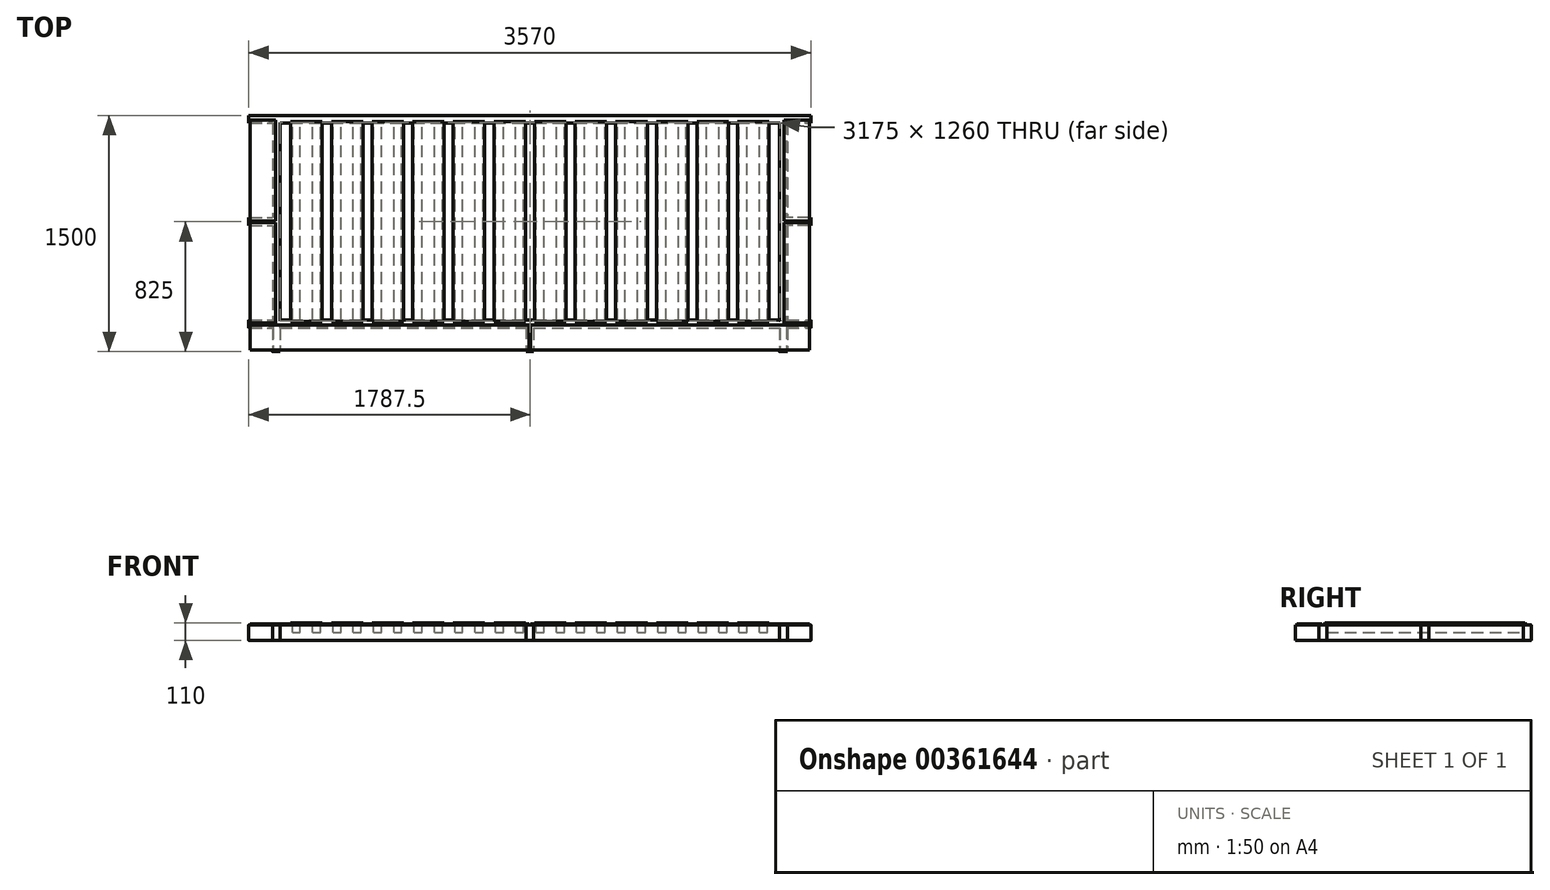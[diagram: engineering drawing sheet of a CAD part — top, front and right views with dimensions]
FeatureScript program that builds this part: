
annotation { "Feature Type Name" : "Feature", "Feature Type Description" : "" }
export const myFeature = defineFeature(function(context is Context, id is Id, definition is map)
    precondition{}
    {
        {
            var Q0;
            Q0=qCreatedBy(makeId("Top.planeOp"),FACE);
            var sketch = newSketch(context, id + "F0", { "sketchPlane" : qUnion([Q0])});
            skLineSegment(sketch, "E0.bottom", {"start": v(0, 0) * mm, "end": v(150, 0) * mm});
            skLineSegment(sketch, "E0.top", {"start": v(0, 50) * mm, "end": v(150, 50) * mm});
            skLineSegment(sketch, "E0.left", {"start": v(0, 0) * mm, "end": v(0, 50) * mm});
            skLineSegment(sketch, "E0.right", {"start": v(3570, 0) * mm, "end": v(3570, 50) * mm});
            skLineSegment(sketch, "E1.bottom", {"start": v(0, 1350) * mm, "end": v(3570, 1350) * mm});
            skLineSegment(sketch, "E1.left", {"start": v(0, 1350) * mm, "end": v(0, 1300) * mm});
            skLineSegment(sketch, "E1.right", {"start": v(3570, 1350) * mm, "end": v(3570, 1300) * mm});
            skLineSegment(sketch, "E2.trimOffspring", {"start": v(0, 1300) * mm, "end": v(150, 1300) * mm});
            skLineSegment(sketch, "E3.top", {"start": v(150, -150) * mm, "end": v(200, -150) * mm});
            skLineSegment(sketch, "E4.top", {"start": v(3370, -150) * mm, "end": v(3420, -150) * mm});
            skLineSegment(sketch, "E4.left", {"start": v(3370, 1300) * mm, "end": v(3370, 50) * mm});
            skLineSegment(sketch, "E4.right", {"start": v(3420, 1300) * mm, "end": v(3420, 50) * mm});
            skLineSegment(sketch, "E5.trimOffspring", {"start": v(3420, 0) * mm, "end": v(3570, 0) * mm});
            skLineSegment(sketch, "E6.trimOffspring", {"start": v(3420, 50) * mm, "end": v(3570, 50) * mm});
            skLineSegment(sketch, "E7.trimOffspring", {"start": v(3370, 0) * mm, "end": v(3370, -150) * mm});
            skLineSegment(sketch, "E8.trimOffspring", {"start": v(3420, 0) * mm, "end": v(3420, -150) * mm});
            skLineSegment(sketch, "E9.trimOffspring", {"start": v(3420, 1300) * mm, "end": v(3570, 1300) * mm});
            skLineSegment(sketch, "E10.trimOffspring", {"start": v(200, 1300) * mm, "end": v(3370, 1300) * mm});
            skLineSegment(sketch, "E11.trimOffspring", {"start": v(200, 50) * mm, "end": v(3370, 50) * mm});
            skLineSegment(sketch, "E12.trimOffspring", {"start": v(200, 0) * mm, "end": v(200, -150) * mm});
            skLineSegment(sketch, "E13.trimOffspring", {"start": v(150, 0) * mm, "end": v(150, -150) * mm});
            skLineSegment(sketch, "E14.trimOffspring", {"start": v(200, 0) * mm, "end": v(1760, 0) * mm});
            skLineSegment(sketch, "E15.bottom", {"start": v(0, 700) * mm, "end": v(150, 700) * mm});
            skLineSegment(sketch, "E15.left", {"start": v(0, 700) * mm, "end": v(0, 675) * mm});
            skPoint(sketch, "E16.startSnap0", {"position": v(1785, 1350) * mm});
            skLineSegment(sketch, "E17.trimOffspring", {"start": v(150, 675) * mm, "end": v(2226.14, 675) * mm, "construction": true});
            skLineSegment(sketch, "E18.MirrorCS", {"start": v(0, 650) * mm, "end": v(0, 675) * mm});
            skLineSegment(sketch, "E19.MirrorCS", {"start": v(0, 650) * mm, "end": v(150, 650) * mm});
            skLineSegment(sketch, "E20.MirrorCS", {"start": v(3570, 650) * mm, "end": v(3420, 650) * mm});
            skLineSegment(sketch, "E21.MirrorCS", {"start": v(3570, 700) * mm, "end": v(3570, 675) * mm});
            skLineSegment(sketch, "E22.MirrorCS", {"start": v(3570, 650) * mm, "end": v(3570, 675) * mm});
            skLineSegment(sketch, "E23.MirrorCS", {"start": v(3570, 700) * mm, "end": v(3420, 700) * mm});
            skLineSegment(sketch, "E24.top", {"start": v(1760, -150) * mm, "end": v(1810, -150) * mm});
            skLineSegment(sketch, "E24.left", {"start": v(1760, 0) * mm, "end": v(1760, -150) * mm});
            skLineSegment(sketch, "E24.right", {"start": v(1810, 0) * mm, "end": v(1810, -150) * mm});
            skLineSegment(sketch, "E25.trimOffspring", {"start": v(1810, 0) * mm, "end": v(3370, 0) * mm});
            skLineSegment(sketch, "E26", {"start": v(150, 1300) * mm, "end": v(150, 50) * mm});
            skLineSegment(sketch, "E27", {"start": v(200, 50) * mm, "end": v(200, 1300) * mm});
            skSolve(sketch);
        }
        {
            var Q0;
            Q0=qSketchRegion(id+"F0",true);
            var Q1;
            {var subQ0=sQuery(id+"F0.wireOp",EDGE,"04053e72-1d3c-4b0a-b337-873e80f4f36b.1.0.0");Q1=makeQuery(id+"F0.imprint","IMPRINT",FACE,{"disambiguationData":[TD([[makeQuery(id+"F0.imprint","IMPRINT",EDGE,{"derivedFrom":subQ0}),1.0]])]});}
            var Q2;
            {var subQ0=sQuery(id+"F0.wireOp",EDGE,"04053e72-1d3c-4b0a-b337-873e80f4f36b.2.0.0");Q2=makeQuery(id+"F0.imprint","IMPRINT",FACE,{"disambiguationData":[TD([[makeQuery(id+"F0.imprint","IMPRINT",EDGE,{"derivedFrom":subQ0}),1.0]])]});}
            var Q3;
            {var subQ0=sQuery(id+"F0.wireOp",EDGE,"04053e72-1d3c-4b0a-b337-873e80f4f36b.3.0.0");Q3=makeQuery(id+"F0.imprint","IMPRINT",FACE,{"disambiguationData":[TD([[makeQuery(id+"F0.imprint","IMPRINT",EDGE,{"derivedFrom":subQ0}),1.0]])]});}
            var Q4;
            {var subQ0=sQuery(id+"F0.wireOp",EDGE,"04053e72-1d3c-4b0a-b337-873e80f4f36b.4.0.0");Q4=makeQuery(id+"F0.imprint","IMPRINT",FACE,{"disambiguationData":[TD([[makeQuery(id+"F0.imprint","IMPRINT",EDGE,{"derivedFrom":subQ0}),1.0]])]});}
            var Q5;
            {var subQ0=sQuery(id+"F0.wireOp",EDGE,"04053e72-1d3c-4b0a-b337-873e80f4f36b.5.0.0");Q5=makeQuery(id+"F0.imprint","IMPRINT",FACE,{"disambiguationData":[TD([[makeQuery(id+"F0.imprint","IMPRINT",EDGE,{"derivedFrom":subQ0}),1.0]])]});}
            var Q6;
            {var subQ0=sQuery(id+"F0.wireOp",EDGE,"04053e72-1d3c-4b0a-b337-873e80f4f36b.6.0.0");Q6=makeQuery(id+"F0.imprint","IMPRINT",FACE,{"disambiguationData":[TD([[makeQuery(id+"F0.imprint","IMPRINT",EDGE,{"derivedFrom":subQ0}),1.0]])]});}
            var Q7;
            {var subQ0=sQuery(id+"F0.wireOp",EDGE,"04053e72-1d3c-4b0a-b337-873e80f4f36b.7.0.0");Q7=makeQuery(id+"F0.imprint","IMPRINT",FACE,{"disambiguationData":[TD([[makeQuery(id+"F0.imprint","IMPRINT",EDGE,{"derivedFrom":subQ0}),1.0]])]});}
            var Q8;
            {var subQ0=sQuery(id+"F0.wireOp",EDGE,"04053e72-1d3c-4b0a-b337-873e80f4f36b.8.0.0");Q8=makeQuery(id+"F0.imprint","IMPRINT",FACE,{"disambiguationData":[TD([[makeQuery(id+"F0.imprint","IMPRINT",EDGE,{"derivedFrom":subQ0}),1.0]])]});}
            var Q9;
            {var subQ0=sQuery(id+"F0.wireOp",EDGE,"04053e72-1d3c-4b0a-b337-873e80f4f36b.9.0.0");Q9=makeQuery(id+"F0.imprint","IMPRINT",FACE,{"disambiguationData":[TD([[makeQuery(id+"F0.imprint","IMPRINT",EDGE,{"derivedFrom":subQ0}),1.0]])]});}
            var Q10;
            {var subQ0=sQuery(id+"F0.wireOp",EDGE,"04053e72-1d3c-4b0a-b337-873e80f4f36b.10.0.0");Q10=makeQuery(id+"F0.imprint","IMPRINT",FACE,{"disambiguationData":[TD([[makeQuery(id+"F0.imprint","IMPRINT",EDGE,{"derivedFrom":subQ0}),1.0]])]});}
            var Q11;
            {var subQ0=sQuery(id+"F0.wireOp",EDGE,"04053e72-1d3c-4b0a-b337-873e80f4f36b.11.0.0");Q11=makeQuery(id+"F0.imprint","IMPRINT",FACE,{"disambiguationData":[TD([[makeQuery(id+"F0.imprint","IMPRINT",EDGE,{"derivedFrom":subQ0}),1.0]])]});}
            var Q12;
            {var subQ0=sQuery(id+"F0.wireOp",EDGE,"04053e72-1d3c-4b0a-b337-873e80f4f36b.12.0.0");Q12=makeQuery(id+"F0.imprint","IMPRINT",FACE,{"disambiguationData":[TD([[makeQuery(id+"F0.imprint","IMPRINT",EDGE,{"derivedFrom":subQ0}),1.0]])]});}
            var Q13;
            {var subQ0=sQuery(id+"F0.wireOp",EDGE,"04053e72-1d3c-4b0a-b337-873e80f4f36b.13.0.0");Q13=makeQuery(id+"F0.imprint","IMPRINT",FACE,{"disambiguationData":[TD([[makeQuery(id+"F0.imprint","IMPRINT",EDGE,{"derivedFrom":subQ0}),1.0]])]});}
            var Q14;
            {var subQ0=sQuery(id+"F0.wireOp",EDGE,"04053e72-1d3c-4b0a-b337-873e80f4f36b.14.0.0");Q14=makeQuery(id+"F0.imprint","IMPRINT",FACE,{"disambiguationData":[TD([[makeQuery(id+"F0.imprint","IMPRINT",EDGE,{"derivedFrom":subQ0}),1.0]])]});}
            var Q15;
            {var subQ0=sQuery(id+"F0.wireOp",EDGE,"04053e72-1d3c-4b0a-b337-873e80f4f36b.15.0.0");Q15=makeQuery(id+"F0.imprint","IMPRINT",FACE,{"disambiguationData":[TD([[makeQuery(id+"F0.imprint","IMPRINT",EDGE,{"derivedFrom":subQ0}),1.0]])]});}
            var Q16;
            {var subQ0=sQuery(id+"F0.wireOp",EDGE,"04053e72-1d3c-4b0a-b337-873e80f4f36b.16.0.0");Q16=makeQuery(id+"F0.imprint","IMPRINT",FACE,{"disambiguationData":[TD([[makeQuery(id+"F0.imprint","IMPRINT",EDGE,{"derivedFrom":subQ0}),1.0]])]});}
            var Q17;
            {var subQ0=sQuery(id+"F0.wireOp",EDGE,"04053e72-1d3c-4b0a-b337-873e80f4f36b.17.0.0");Q17=makeQuery(id+"F0.imprint","IMPRINT",FACE,{"disambiguationData":[TD([[makeQuery(id+"F0.imprint","IMPRINT",EDGE,{"derivedFrom":subQ0}),1.0]])]});}
            var Q18;
            {var subQ0=sQuery(id+"F0.wireOp",EDGE,"04053e72-1d3c-4b0a-b337-873e80f4f36b.18.0.0");Q18=makeQuery(id+"F0.imprint","IMPRINT",FACE,{"disambiguationData":[TD([[makeQuery(id+"F0.imprint","IMPRINT",EDGE,{"derivedFrom":subQ0}),1.0]])]});}
            var Q19;
            {var subQ0=sQuery(id+"F0.wireOp",EDGE,"04053e72-1d3c-4b0a-b337-873e80f4f36b.19.0.0");Q19=makeQuery(id+"F0.imprint","IMPRINT",FACE,{"disambiguationData":[TD([[makeQuery(id+"F0.imprint","IMPRINT",EDGE,{"derivedFrom":subQ0}),1.0]])]});}
            var Q20;
            {var subQ0=sQuery(id+"F0.wireOp",EDGE,"83652a9d-b2ed-44b6-aa75-f454ae2646cd.0.20.0");Q20=makeQuery(id+"F0.imprint","IMPRINT",FACE,{"disambiguationData":[TD([[makeQuery(id+"F0.imprint","IMPRINT",EDGE,{"derivedFrom":subQ0}),1.0]])]});}
            var Q21;
            {var subQ0=sQuery(id+"F0.wireOp",EDGE,"83652a9d-b2ed-44b6-aa75-f454ae2646cd.0.21.0");Q21=makeQuery(id+"F0.imprint","IMPRINT",FACE,{"disambiguationData":[TD([[makeQuery(id+"F0.imprint","IMPRINT",EDGE,{"derivedFrom":subQ0}),1.0]])]});}
            var Q22;
            {var subQ0=sQuery(id+"F0.wireOp",EDGE,"83652a9d-b2ed-44b6-aa75-f454ae2646cd.0.22.0");Q22=makeQuery(id+"F0.imprint","IMPRINT",FACE,{"disambiguationData":[TD([[makeQuery(id+"F0.imprint","IMPRINT",EDGE,{"derivedFrom":subQ0}),1.0]])]});}
            var Q23;
            {var subQ0=sQuery(id+"F0.wireOp",EDGE,"83652a9d-b2ed-44b6-aa75-f454ae2646cd.0.23.0");Q23=makeQuery(id+"F0.imprint","IMPRINT",FACE,{"disambiguationData":[TD([[makeQuery(id+"F0.imprint","IMPRINT",EDGE,{"derivedFrom":subQ0}),1.0]])]});}
            var Q24;
            {var subQ0=sQuery(id+"F0.wireOp",EDGE,"83652a9d-b2ed-44b6-aa75-f454ae2646cd.0.24.0");Q24=makeQuery(id+"F0.imprint","IMPRINT",FACE,{"disambiguationData":[TD([[makeQuery(id+"F0.imprint","IMPRINT",EDGE,{"derivedFrom":subQ0}),1.0]])]});}
            var Q25;
            {var subQ0=sQuery(id+"F0.wireOp",EDGE,"83652a9d-b2ed-44b6-aa75-f454ae2646cd.0.25.0");Q25=makeQuery(id+"F0.imprint","IMPRINT",FACE,{"disambiguationData":[TD([[makeQuery(id+"F0.imprint","IMPRINT",EDGE,{"derivedFrom":subQ0}),1.0]])]});}
            extrude(context, id + "F1", {"entities" : qUnion([Q0, Q1, Q2, Q3, Q4, Q5, Q6, Q7, Q8, Q9, Q10, Q11, Q12, Q13, Q14, Q15, Q16, Q17, Q18, Q19, Q20, Q21, Q22, Q23, Q24, Q25]), "oppositeDirection" : true, "depth" : 100 * mm});
        }
        {
            var Q0;
            Q0=makeQuery(id+"FPwb0Jo6nws5QIE_0.opExtrude","CAP_EDGE",EDGE,{"disambiguationData":[OSD([sQuery(id+"F0.wireOp",EDGE,"E14.trimOffspring")])],"isStart":false});
            var Q1;
            Q1=makeQuery(id+"FPwb0Jo6nws5QIE_0.opExtrude","CAP_EDGE",EDGE,{"disambiguationData":[OSD([sQuery(id+"F0.wireOp",EDGE,"E7.trimOffspring")])],"isStart":false});
            var Q2;
            Q2=makeQuery(id+"FPwb0Jo6nws5QIE_0.opExtrude","CAP_EDGE",EDGE,{"disambiguationData":[OSD([sQuery(id+"F0.wireOp",EDGE,"E5.trimOffspring")])],"isStart":false});
            var Q3;
            Q3=makeQuery(id+"FPwb0Jo6nws5QIE_0.opExtrude","CAP_EDGE",EDGE,{"disambiguationData":[OSD([sQuery(id+"F0.wireOp",EDGE,"E8.trimOffspring")])],"isStart":false});
            var Q4;
            Q4=makeQuery(id+"FPwb0Jo6nws5QIE_0.opExtrude","CAP_EDGE",EDGE,{"disambiguationData":[OSD([sQuery(id+"F0.wireOp",EDGE,"E6.trimOffspring")])],"isStart":false});
            var Q5;
            Q5=makeQuery(id+"FPwb0Jo6nws5QIE_0.opExtrude","CAP_EDGE",EDGE,{"disambiguationData":[OSD([sQuery(id+"F0.wireOp",EDGE,"E4.right")])],"isStart":false});
            var Q6;
            Q6=makeQuery(id+"FPwb0Jo6nws5QIE_0.opExtrude","CAP_EDGE",EDGE,{"disambiguationData":[OSD([sQuery(id+"F0.wireOp",EDGE,"E4.left")])],"isStart":false});
            var Q7;
            Q7=makeQuery(id+"FPwb0Jo6nws5QIE_0.opExtrude","CAP_EDGE",EDGE,{"disambiguationData":[OSD([sQuery(id+"F0.wireOp",EDGE,"E11.trimOffspring")])],"isStart":false});
            var Q8;
            Q8=makeQuery(id+"FPwb0Jo6nws5QIE_0.opExtrude","CAP_EDGE",EDGE,{"disambiguationData":[OSD([sQuery(id+"F0.wireOp",EDGE,"E10.trimOffspring")])],"isStart":false});
            var Q9;
            Q9=makeQuery(id+"FPwb0Jo6nws5QIE_0.opExtrude","CAP_EDGE",EDGE,{"disambiguationData":[OSD([sQuery(id+"F0.wireOp",EDGE,"E1.bottom")])],"isStart":false});
            var Q10;
            Q10=makeQuery(id+"FPwb0Jo6nws5QIE_0.opExtrude","CAP_EDGE",EDGE,{"disambiguationData":[OSD([sQuery(id+"F0.wireOp",EDGE,"E9.trimOffspring")])],"isStart":false});
            var Q11;
            Q11=makeQuery(id+"FPwb0Jo6nws5QIE_0.opExtrude","CAP_EDGE",EDGE,{"disambiguationData":[OSD([sQuery(id+"F0.wireOp",EDGE,"E3.right")])],"isStart":false});
            var Q12;
            Q12=makeQuery(id+"FPwb0Jo6nws5QIE_0.opExtrude","CAP_EDGE",EDGE,{"disambiguationData":[OSD([sQuery(id+"F0.wireOp",EDGE,"E2.trimOffspring")])],"isStart":false});
            var Q13;
            Q13=makeQuery(id+"FPwb0Jo6nws5QIE_0.opExtrude","CAP_EDGE",EDGE,{"disambiguationData":[OSD([sQuery(id+"F0.wireOp",EDGE,"E3.left")])],"isStart":false});
            var Q14;
            Q14=makeQuery(id+"FPwb0Jo6nws5QIE_0.opExtrude","CAP_EDGE",EDGE,{"disambiguationData":[OSD([sQuery(id+"F0.wireOp",EDGE,"E0.top")])],"isStart":false});
            var Q15;
            Q15=makeQuery(id+"FPwb0Jo6nws5QIE_0.opExtrude","CAP_EDGE",EDGE,{"disambiguationData":[OSD([sQuery(id+"F0.wireOp",EDGE,"E0.bottom")])],"isStart":false});
            var Q16;
            Q16=makeQuery(id+"FPwb0Jo6nws5QIE_0.opExtrude","CAP_EDGE",EDGE,{"disambiguationData":[OSD([sQuery(id+"F0.wireOp",EDGE,"E13.trimOffspring")])],"isStart":false});
            var Q17;
            Q17=makeQuery(id+"FPwb0Jo6nws5QIE_0.opExtrude","CAP_EDGE",EDGE,{"disambiguationData":[OSD([sQuery(id+"F0.wireOp",EDGE,"E12.trimOffspring")])],"isStart":false});
            var Q18;
            Q18=makeQuery(id+"F1.opExtrude","CAP_EDGE",EDGE,{"disambiguationData":[OSD([sQuery(id+"F0.wireOp",EDGE,"E2.trimOffspring")])],"isStart":true});
            var Q19;
            Q19=makeQuery(id+"F1.opExtrude","CAP_EDGE",EDGE,{"disambiguationData":[OSD([sQuery(id+"F0.wireOp",EDGE,"E1.bottom")])],"isStart":true});
            var Q20;
            Q20=makeQuery(id+"F1.opExtrude","CAP_EDGE",EDGE,{"disambiguationData":[OSD([sQuery(id+"F0.wireOp",EDGE,"E10.trimOffspring")])],"isStart":true});
            var Q21;
            Q21=makeQuery(id+"F1.opExtrude","CAP_EDGE",EDGE,{"disambiguationData":[OSD([sQuery(id+"F0.wireOp",EDGE,"E3.right")])],"isStart":true});
            var Q22;
            Q22=makeQuery(id+"F1.opExtrude","CAP_EDGE",EDGE,{"disambiguationData":[OSD([sQuery(id+"F0.wireOp",EDGE,"E3.left")])],"isStart":true});
            var Q23;
            Q23=makeQuery(id+"F1.opExtrude","CAP_EDGE",EDGE,{"disambiguationData":[OSD([sQuery(id+"F0.wireOp",EDGE,"E14.trimOffspring")])],"isStart":true});
            var Q24;
            Q24=makeQuery(id+"F1.opExtrude","CAP_EDGE",EDGE,{"disambiguationData":[OSD([sQuery(id+"F0.wireOp",EDGE,"E11.trimOffspring")])],"isStart":true});
            var Q25;
            Q25=makeQuery(id+"F1.opExtrude","CAP_EDGE",EDGE,{"disambiguationData":[OSD([sQuery(id+"F0.wireOp",EDGE,"E0.top")])],"isStart":true});
            var Q26;
            Q26=makeQuery(id+"F1.opExtrude","CAP_EDGE",EDGE,{"disambiguationData":[OSD([sQuery(id+"F0.wireOp",EDGE,"E0.bottom")])],"isStart":true});
            var Q27;
            Q27=makeQuery(id+"F1.opExtrude","CAP_EDGE",EDGE,{"disambiguationData":[OSD([sQuery(id+"F0.wireOp",EDGE,"E13.trimOffspring")])],"isStart":true});
            var Q28;
            Q28=makeQuery(id+"F1.opExtrude","CAP_EDGE",EDGE,{"disambiguationData":[OSD([sQuery(id+"F0.wireOp",EDGE,"E4.left")])],"isStart":true});
            var Q29;
            Q29=makeQuery(id+"F1.opExtrude","CAP_EDGE",EDGE,{"disambiguationData":[OSD([sQuery(id+"F0.wireOp",EDGE,"E4.right")])],"isStart":true});
            var Q30;
            Q30=makeQuery(id+"F1.opExtrude","CAP_EDGE",EDGE,{"disambiguationData":[OSD([sQuery(id+"F0.wireOp",EDGE,"E6.trimOffspring")])],"isStart":true});
            var Q31;
            Q31=makeQuery(id+"F1.opExtrude","CAP_EDGE",EDGE,{"disambiguationData":[OSD([sQuery(id+"F0.wireOp",EDGE,"E5.trimOffspring")])],"isStart":true});
            var Q32;
            Q32=makeQuery(id+"F1.opExtrude","CAP_EDGE",EDGE,{"disambiguationData":[OSD([sQuery(id+"F0.wireOp",EDGE,"E8.trimOffspring")])],"isStart":true});
            var Q33;
            Q33=makeQuery(id+"F1.opExtrude","CAP_EDGE",EDGE,{"disambiguationData":[OSD([sQuery(id+"F0.wireOp",EDGE,"E7.trimOffspring")])],"isStart":true});
            var Q34;
            Q34=makeQuery(id+"F1.opExtrude","CAP_EDGE",EDGE,{"disambiguationData":[OSD([sQuery(id+"F0.wireOp",EDGE,"E9.trimOffspring")])],"isStart":true});
            fillet(context, id + "F2", {"entities" : qUnion([Q0, Q1, Q2, Q3, Q4, Q5, Q6, Q7, Q8, Q9, Q10, Q11, Q12, Q13, Q14, Q15, Q16, Q17, Q18, Q19, Q20, Q21, Q22, Q23, Q24, Q25, Q26, Q27, Q28, Q29, Q30, Q31, Q32, Q33, Q34]), "radius" : 5 * mm, "tangentPropagation" : true, "allowEdgeOverflow" : false});
        }
        {
            var Q0;
            Q0=makeQuery(id+"F1.opExtrude","CAP_EDGE",EDGE,{"disambiguationData":[OSD([sQuery(id+"F0.wireOp",EDGE,"E6.trimOffspring")])],"isStart":false});
            var Q1;
            Q1=makeQuery(id+"F1.opExtrude","CAP_EDGE",EDGE,{"disambiguationData":[OSD([sQuery(id+"F0.wireOp",EDGE,"E11.trimOffspring")])],"isStart":false});
            var Q2;
            Q2=makeQuery(id+"F1.opExtrude","CAP_EDGE",EDGE,{"disambiguationData":[OSD([sQuery(id+"F0.wireOp",EDGE,"E4.left")])],"isStart":false});
            var Q3;
            Q3=makeQuery(id+"F1.opExtrude","CAP_EDGE",EDGE,{"disambiguationData":[OSD([sQuery(id+"F0.wireOp",EDGE,"E4.right")])],"isStart":false});
            var Q4;
            Q4=makeQuery(id+"F1.opExtrude","CAP_EDGE",EDGE,{"disambiguationData":[OSD([sQuery(id+"F0.wireOp",EDGE,"E8.trimOffspring")])],"isStart":false});
            var Q5;
            Q5=makeQuery(id+"F1.opExtrude","CAP_EDGE",EDGE,{"disambiguationData":[OSD([sQuery(id+"F0.wireOp",EDGE,"E7.trimOffspring")])],"isStart":false});
            var Q6;
            Q6=makeQuery(id+"F1.opExtrude","CAP_EDGE",EDGE,{"disambiguationData":[OSD([sQuery(id+"F0.wireOp",EDGE,"E5.trimOffspring")])],"isStart":false});
            var Q7;
            Q7=makeQuery(id+"F1.opExtrude","CAP_EDGE",EDGE,{"disambiguationData":[OSD([sQuery(id+"F0.wireOp",EDGE,"E14.trimOffspring")])],"isStart":false});
            var Q8;
            Q8=makeQuery(id+"F1.opExtrude","CAP_EDGE",EDGE,{"disambiguationData":[OSD([sQuery(id+"F0.wireOp",EDGE,"E12.trimOffspring")])],"isStart":false});
            var Q9;
            Q9=makeQuery(id+"F1.opExtrude","CAP_EDGE",EDGE,{"disambiguationData":[OSD([sQuery(id+"F0.wireOp",EDGE,"E3.left")])],"isStart":false});
            var Q10;
            Q10=makeQuery(id+"F1.opExtrude","CAP_EDGE",EDGE,{"disambiguationData":[OSD([sQuery(id+"F0.wireOp",EDGE,"E3.right")])],"isStart":false});
            var Q11;
            Q11=makeQuery(id+"F1.opExtrude","CAP_EDGE",EDGE,{"disambiguationData":[OSD([sQuery(id+"F0.wireOp",EDGE,"E0.top")])],"isStart":false});
            var Q12;
            Q12=makeQuery(id+"F1.opExtrude","CAP_EDGE",EDGE,{"disambiguationData":[OSD([sQuery(id+"F0.wireOp",EDGE,"E0.bottom")])],"isStart":false});
            var Q13;
            Q13=makeQuery(id+"F1.opExtrude","CAP_EDGE",EDGE,{"disambiguationData":[OSD([sQuery(id+"F0.wireOp",EDGE,"E13.trimOffspring")])],"isStart":false});
            var Q14;
            Q14=makeQuery(id+"F1.opExtrude","CAP_EDGE",EDGE,{"disambiguationData":[OSD([sQuery(id+"F0.wireOp",EDGE,"E2.trimOffspring")])],"isStart":false});
            var Q15;
            Q15=makeQuery(id+"F1.opExtrude","CAP_EDGE",EDGE,{"disambiguationData":[OSD([sQuery(id+"F0.wireOp",EDGE,"E1.bottom")])],"isStart":false});
            var Q16;
            Q16=makeQuery(id+"F1.opExtrude","CAP_EDGE",EDGE,{"disambiguationData":[OSD([sQuery(id+"F0.wireOp",EDGE,"E10.trimOffspring")])],"isStart":false});
            var Q17;
            Q17=makeQuery(id+"F1.opExtrude","CAP_EDGE",EDGE,{"disambiguationData":[OSD([sQuery(id+"F0.wireOp",EDGE,"E9.trimOffspring")])],"isStart":false});
            fillet(context, id + "F3", {"entities" : qUnion([Q0, Q1, Q2, Q3, Q4, Q5, Q6, Q7, Q8, Q9, Q10, Q11, Q12, Q13, Q14, Q15, Q16, Q17]), "radius" : 5 * mm, "tangentPropagation" : true, "allowEdgeOverflow" : false});
        }
        {
            var Q0;
            Q0=qCreatedBy(makeId("Top.planeOp"),FACE);
            var sketch = newSketch(context, id + "F4", { "sketchPlane" : qUnion([Q0])});
            skPoint(sketch, "E28.firstSnap0", {"position": v(10, 20) * mm});
            skLineSegment(sketch, "E28.bottom", {"start": v(1780, 20) * mm, "end": v(10, 20) * mm});
            skLineSegment(sketch, "E28.top", {"start": v(1780, -140) * mm, "end": v(10, -140) * mm});
            skLineSegment(sketch, "E28.left", {"start": v(1780, 20) * mm, "end": v(1780, -140) * mm});
            skLineSegment(sketch, "E28.right", {"start": v(10, 20) * mm, "end": v(10, -140) * mm});
            skLineSegment(sketch, "E29.bottom", {"start": v(1790, 20) * mm, "end": v(3560, 20) * mm});
            skLineSegment(sketch, "E29.top", {"start": v(1790, -140) * mm, "end": v(3560, -140) * mm});
            skLineSegment(sketch, "E29.left", {"start": v(1790, 20) * mm, "end": v(1790, -140) * mm});
            skLineSegment(sketch, "E29.right", {"start": v(3560, 20) * mm, "end": v(3560, -140) * mm});
            skLineSegment(sketch, "E30.bottom", {"start": v(10, 1320) * mm, "end": v(170, 1320) * mm});
            skLineSegment(sketch, "E30.top", {"start": v(10, 680) * mm, "end": v(170, 680) * mm});
            skLineSegment(sketch, "E30.left", {"start": v(10, 1320) * mm, "end": v(10, 680) * mm});
            skLineSegment(sketch, "E30.right", {"start": v(170, 1320) * mm, "end": v(170, 680) * mm});
            skLineSegment(sketch, "E31.bottom", {"start": v(10, 670) * mm, "end": v(170, 670) * mm});
            skLineSegment(sketch, "E31.top", {"start": v(10, 30) * mm, "end": v(170, 30) * mm});
            skLineSegment(sketch, "E31.left", {"start": v(10, 670) * mm, "end": v(10, 30) * mm});
            skLineSegment(sketch, "E31.right", {"start": v(170, 670) * mm, "end": v(170, 30) * mm});
            skLineSegment(sketch, "E32.bottom", {"start": v(3400, 1320) * mm, "end": v(3560, 1320) * mm});
            skLineSegment(sketch, "E32.top", {"start": v(3400, 680) * mm, "end": v(3560, 680) * mm});
            skLineSegment(sketch, "E32.left", {"start": v(3400, 1320) * mm, "end": v(3400, 680) * mm});
            skLineSegment(sketch, "E32.right", {"start": v(3560, 1320) * mm, "end": v(3560, 680) * mm});
            skLineSegment(sketch, "E33.bottom", {"start": v(3400, 670) * mm, "end": v(3560, 670) * mm});
            skLineSegment(sketch, "E33.top", {"start": v(3400, 30) * mm, "end": v(3560, 30) * mm});
            skLineSegment(sketch, "E33.left", {"start": v(3400, 670) * mm, "end": v(3400, 30) * mm});
            skLineSegment(sketch, "E33.right", {"start": v(3560, 670) * mm, "end": v(3560, 30) * mm});
            skSolve(sketch);
        }
        {
            var Q0;
            Q0=qSketchRegion(id+"F4",true);
            extrude(context, id + "F5", {"entities" : qUnion([Q0]), "operationType" : NewBodyOperationType.ADD, "depth" : 5 * mm});
        }
        {
            var Q0;
            Q0=qCreatedBy(makeId("Top.planeOp"),FACE);
            var sketch = newSketch(context, id + "F6", { "sketchPlane" : qUnion([Q0])});
            skLineSegment(sketch, "E34.bottom", {"start": v(277, 50) * mm, "end": v(327, 50) * mm});
            skLineSegment(sketch, "E34.top", {"start": v(277, 1300) * mm, "end": v(327, 1300) * mm});
            skLineSegment(sketch, "E34.left", {"start": v(277, 50) * mm, "end": v(277, 1300) * mm});
            skLineSegment(sketch, "E34.right", {"start": v(327, 50) * mm, "end": v(327, 1300) * mm});
            skLineSegment(sketch, "E35.1.0.0", {"start": v(406, 50) * mm, "end": v(406, 1300) * mm});
            skLineSegment(sketch, "E35.1.0.1", {"start": v(406, 1300) * mm, "end": v(456, 1300) * mm});
            skLineSegment(sketch, "E35.1.0.2", {"start": v(456, 50) * mm, "end": v(456, 1300) * mm});
            skLineSegment(sketch, "E35.1.0.3", {"start": v(406, 50) * mm, "end": v(456, 50) * mm});
            skLineSegment(sketch, "E35.2.0.0", {"start": v(535, 50) * mm, "end": v(535, 1300) * mm});
            skLineSegment(sketch, "E35.2.0.1", {"start": v(535, 1300) * mm, "end": v(585, 1300) * mm});
            skLineSegment(sketch, "E35.2.0.2", {"start": v(585, 50) * mm, "end": v(585, 1300) * mm});
            skLineSegment(sketch, "E35.2.0.3", {"start": v(535, 50) * mm, "end": v(585, 50) * mm});
            skLineSegment(sketch, "E35.3.0.0", {"start": v(664, 50) * mm, "end": v(664, 1300) * mm});
            skLineSegment(sketch, "E35.3.0.1", {"start": v(664, 1300) * mm, "end": v(714, 1300) * mm});
            skLineSegment(sketch, "E35.3.0.2", {"start": v(714, 50) * mm, "end": v(714, 1300) * mm});
            skLineSegment(sketch, "E35.3.0.3", {"start": v(664, 50) * mm, "end": v(714, 50) * mm});
            skLineSegment(sketch, "E35.4.0.0", {"start": v(793, 50) * mm, "end": v(793, 1300) * mm});
            skLineSegment(sketch, "E35.4.0.1", {"start": v(793, 1300) * mm, "end": v(843, 1300) * mm});
            skLineSegment(sketch, "E35.4.0.2", {"start": v(843, 50) * mm, "end": v(843, 1300) * mm});
            skLineSegment(sketch, "E35.4.0.3", {"start": v(793, 50) * mm, "end": v(843, 50) * mm});
            skLineSegment(sketch, "E35.5.0.0", {"start": v(922, 50) * mm, "end": v(922, 1300) * mm});
            skLineSegment(sketch, "E35.5.0.1", {"start": v(922, 1300) * mm, "end": v(972, 1300) * mm});
            skLineSegment(sketch, "E35.5.0.2", {"start": v(972, 50) * mm, "end": v(972, 1300) * mm});
            skLineSegment(sketch, "E35.5.0.3", {"start": v(922, 50) * mm, "end": v(972, 50) * mm});
            skLineSegment(sketch, "E35.6.0.0", {"start": v(1051, 50) * mm, "end": v(1051, 1300) * mm});
            skLineSegment(sketch, "E35.6.0.1", {"start": v(1051, 1300) * mm, "end": v(1101, 1300) * mm});
            skLineSegment(sketch, "E35.6.0.2", {"start": v(1101, 50) * mm, "end": v(1101, 1300) * mm});
            skLineSegment(sketch, "E35.6.0.3", {"start": v(1051, 50) * mm, "end": v(1101, 50) * mm});
            skLineSegment(sketch, "E35.7.0.0", {"start": v(1180, 50) * mm, "end": v(1180, 1300) * mm});
            skLineSegment(sketch, "E35.7.0.1", {"start": v(1180, 1300) * mm, "end": v(1230, 1300) * mm});
            skLineSegment(sketch, "E35.7.0.2", {"start": v(1230, 50) * mm, "end": v(1230, 1300) * mm});
            skLineSegment(sketch, "E35.7.0.3", {"start": v(1180, 50) * mm, "end": v(1230, 50) * mm});
            skLineSegment(sketch, "E35.8.0.0", {"start": v(1309, 50) * mm, "end": v(1309, 1300) * mm});
            skLineSegment(sketch, "E35.8.0.1", {"start": v(1309, 1300) * mm, "end": v(1359, 1300) * mm});
            skLineSegment(sketch, "E35.8.0.2", {"start": v(1359, 50) * mm, "end": v(1359, 1300) * mm});
            skLineSegment(sketch, "E35.8.0.3", {"start": v(1309, 50) * mm, "end": v(1359, 50) * mm});
            skLineSegment(sketch, "E35.9.0.0", {"start": v(1438, 50) * mm, "end": v(1438, 1300) * mm});
            skLineSegment(sketch, "E35.9.0.1", {"start": v(1438, 1300) * mm, "end": v(1488, 1300) * mm});
            skLineSegment(sketch, "E35.9.0.2", {"start": v(1488, 50) * mm, "end": v(1488, 1300) * mm});
            skLineSegment(sketch, "E35.9.0.3", {"start": v(1438, 50) * mm, "end": v(1488, 50) * mm});
            skLineSegment(sketch, "E35.10.0.0", {"start": v(1567, 50) * mm, "end": v(1567, 1300) * mm});
            skLineSegment(sketch, "E35.10.0.1", {"start": v(1567, 1300) * mm, "end": v(1617, 1300) * mm});
            skLineSegment(sketch, "E35.10.0.2", {"start": v(1617, 50) * mm, "end": v(1617, 1300) * mm});
            skLineSegment(sketch, "E35.10.0.3", {"start": v(1567, 50) * mm, "end": v(1617, 50) * mm});
            skLineSegment(sketch, "E35.11.0.0", {"start": v(1696, 50) * mm, "end": v(1696, 1300) * mm});
            skLineSegment(sketch, "E35.11.0.1", {"start": v(1696, 1300) * mm, "end": v(1746, 1300) * mm});
            skLineSegment(sketch, "E35.11.0.2", {"start": v(1746, 50) * mm, "end": v(1746, 1300) * mm});
            skLineSegment(sketch, "E35.11.0.3", {"start": v(1696, 50) * mm, "end": v(1746, 50) * mm});
            skLineSegment(sketch, "E35.12.0.0", {"start": v(1825, 50) * mm, "end": v(1825, 1300) * mm});
            skLineSegment(sketch, "E35.12.0.1", {"start": v(1825, 1300) * mm, "end": v(1875, 1300) * mm});
            skLineSegment(sketch, "E35.12.0.2", {"start": v(1875, 50) * mm, "end": v(1875, 1300) * mm});
            skLineSegment(sketch, "E35.12.0.3", {"start": v(1825, 50) * mm, "end": v(1875, 50) * mm});
            skLineSegment(sketch, "E35.13.0.0", {"start": v(1954, 50) * mm, "end": v(1954, 1300) * mm});
            skLineSegment(sketch, "E35.13.0.1", {"start": v(1954, 1300) * mm, "end": v(2004, 1300) * mm});
            skLineSegment(sketch, "E35.13.0.2", {"start": v(2004, 50) * mm, "end": v(2004, 1300) * mm});
            skLineSegment(sketch, "E35.13.0.3", {"start": v(1954, 50) * mm, "end": v(2004, 50) * mm});
            skLineSegment(sketch, "E35.14.0.0", {"start": v(2083, 50) * mm, "end": v(2083, 1300) * mm});
            skLineSegment(sketch, "E35.14.0.1", {"start": v(2083, 1300) * mm, "end": v(2133, 1300) * mm});
            skLineSegment(sketch, "E35.14.0.2", {"start": v(2133, 50) * mm, "end": v(2133, 1300) * mm});
            skLineSegment(sketch, "E35.14.0.3", {"start": v(2083, 50) * mm, "end": v(2133, 50) * mm});
            skLineSegment(sketch, "E35.15.0.0", {"start": v(2212, 50) * mm, "end": v(2212, 1300) * mm});
            skLineSegment(sketch, "E35.15.0.1", {"start": v(2212, 1300) * mm, "end": v(2262, 1300) * mm});
            skLineSegment(sketch, "E35.15.0.2", {"start": v(2262, 50) * mm, "end": v(2262, 1300) * mm});
            skLineSegment(sketch, "E35.15.0.3", {"start": v(2212, 50) * mm, "end": v(2262, 50) * mm});
            skLineSegment(sketch, "E35.16.0.0", {"start": v(2341, 50) * mm, "end": v(2341, 1300) * mm});
            skLineSegment(sketch, "E35.16.0.1", {"start": v(2341, 1300) * mm, "end": v(2391, 1300) * mm});
            skLineSegment(sketch, "E35.16.0.2", {"start": v(2391, 50) * mm, "end": v(2391, 1300) * mm});
            skLineSegment(sketch, "E35.16.0.3", {"start": v(2341, 50) * mm, "end": v(2391, 50) * mm});
            skLineSegment(sketch, "E35.17.0.0", {"start": v(2470, 50) * mm, "end": v(2470, 1300) * mm});
            skLineSegment(sketch, "E35.17.0.1", {"start": v(2470, 1300) * mm, "end": v(2520, 1300) * mm});
            skLineSegment(sketch, "E35.17.0.2", {"start": v(2520, 50) * mm, "end": v(2520, 1300) * mm});
            skLineSegment(sketch, "E35.17.0.3", {"start": v(2470, 50) * mm, "end": v(2520, 50) * mm});
            skLineSegment(sketch, "E35.18.0.0", {"start": v(2599, 50) * mm, "end": v(2599, 1300) * mm});
            skLineSegment(sketch, "E35.18.0.1", {"start": v(2599, 1300) * mm, "end": v(2649, 1300) * mm});
            skLineSegment(sketch, "E35.18.0.2", {"start": v(2649, 50) * mm, "end": v(2649, 1300) * mm});
            skLineSegment(sketch, "E35.18.0.3", {"start": v(2599, 50) * mm, "end": v(2649, 50) * mm});
            skLineSegment(sketch, "E35.19.0.0", {"start": v(2728, 50) * mm, "end": v(2728, 1300) * mm});
            skLineSegment(sketch, "E35.19.0.1", {"start": v(2728, 1300) * mm, "end": v(2778, 1300) * mm});
            skLineSegment(sketch, "E35.19.0.2", {"start": v(2778, 50) * mm, "end": v(2778, 1300) * mm});
            skLineSegment(sketch, "E35.19.0.3", {"start": v(2728, 50) * mm, "end": v(2778, 50) * mm});
            skLineSegment(sketch, "E35.20.0.0", {"start": v(2857, 50) * mm, "end": v(2857, 1300) * mm});
            skLineSegment(sketch, "E35.20.0.1", {"start": v(2857, 1300) * mm, "end": v(2907, 1300) * mm});
            skLineSegment(sketch, "E35.20.0.2", {"start": v(2907, 50) * mm, "end": v(2907, 1300) * mm});
            skLineSegment(sketch, "E35.20.0.3", {"start": v(2857, 50) * mm, "end": v(2907, 50) * mm});
            skLineSegment(sketch, "E35.21.0.0", {"start": v(2986, 50) * mm, "end": v(2986, 1300) * mm});
            skLineSegment(sketch, "E35.21.0.1", {"start": v(2986, 1300) * mm, "end": v(3036, 1300) * mm});
            skLineSegment(sketch, "E35.21.0.2", {"start": v(3036, 50) * mm, "end": v(3036, 1300) * mm});
            skLineSegment(sketch, "E35.21.0.3", {"start": v(2986, 50) * mm, "end": v(3036, 50) * mm});
            skLineSegment(sketch, "E35.22.0.0", {"start": v(3115, 50) * mm, "end": v(3115, 1300) * mm});
            skLineSegment(sketch, "E35.22.0.1", {"start": v(3115, 1300) * mm, "end": v(3165, 1300) * mm});
            skLineSegment(sketch, "E35.22.0.2", {"start": v(3165, 50) * mm, "end": v(3165, 1300) * mm});
            skLineSegment(sketch, "E35.22.0.3", {"start": v(3115, 50) * mm, "end": v(3165, 50) * mm});
            skLineSegment(sketch, "E35.23.0.0", {"start": v(3244, 50) * mm, "end": v(3244, 1300) * mm});
            skLineSegment(sketch, "E35.23.0.1", {"start": v(3244, 1300) * mm, "end": v(3294, 1300) * mm});
            skLineSegment(sketch, "E35.23.0.2", {"start": v(3294, 50) * mm, "end": v(3294, 1300) * mm});
            skLineSegment(sketch, "E35.23.0.3", {"start": v(3244, 50) * mm, "end": v(3294, 50) * mm});
            skLineSegment(sketch, "E35.direction1", {"start": v(277, 50) * mm, "end": v(406, 50) * mm, "construction": true});
            skSolve(sketch);
        }
        {
            var Q0;
            Q0 = qSketchRegion(id + "F6", true);
            extrude(context, id + "F7", {"entities" : qUnion([Q0]), "oppositeDirection" : true, "depth" : 50 * mm});
        }
        {
            var Q0;
            Q0=qCreatedBy(makeId("Top.planeOp"),FACE);
            var sketch = newSketch(context, id + "F8", { "sketchPlane" : qUnion([Q0])});
            skLineSegment(sketch, "E36.bottom", {"start": v(267, 1310) * mm, "end": v(467, 1310) * mm});
            skLineSegment(sketch, "E36.top", {"start": v(267, 40) * mm, "end": v(467, 40) * mm});
            skLineSegment(sketch, "E36.left", {"start": v(267, 1310) * mm, "end": v(267, 40) * mm});
            skLineSegment(sketch, "E36.right", {"start": v(467, 1310) * mm, "end": v(467, 40) * mm});
            skLineSegment(sketch, "E37.1.0.0", {"start": v(525, 1310) * mm, "end": v(525, 40) * mm});
            skLineSegment(sketch, "E37.1.0.1", {"start": v(525, 40) * mm, "end": v(725, 40) * mm});
            skLineSegment(sketch, "E37.1.0.2", {"start": v(525, 1310) * mm, "end": v(725, 1310) * mm});
            skLineSegment(sketch, "E37.1.0.3", {"start": v(725, 1310) * mm, "end": v(725, 40) * mm});
            skLineSegment(sketch, "E37.2.0.0", {"start": v(783, 1310) * mm, "end": v(783, 40) * mm});
            skLineSegment(sketch, "E37.2.0.1", {"start": v(783, 40) * mm, "end": v(983, 40) * mm});
            skLineSegment(sketch, "E37.2.0.2", {"start": v(783, 1310) * mm, "end": v(983, 1310) * mm});
            skLineSegment(sketch, "E37.2.0.3", {"start": v(983, 1310) * mm, "end": v(983, 40) * mm});
            skLineSegment(sketch, "E37.3.0.0", {"start": v(1041, 1310) * mm, "end": v(1041, 40) * mm});
            skLineSegment(sketch, "E37.3.0.1", {"start": v(1041, 40) * mm, "end": v(1241, 40) * mm});
            skLineSegment(sketch, "E37.3.0.2", {"start": v(1041, 1310) * mm, "end": v(1241, 1310) * mm});
            skLineSegment(sketch, "E37.3.0.3", {"start": v(1241, 1310) * mm, "end": v(1241, 40) * mm});
            skLineSegment(sketch, "E37.4.0.0", {"start": v(1299, 1310) * mm, "end": v(1299, 40) * mm});
            skLineSegment(sketch, "E37.4.0.1", {"start": v(1299, 40) * mm, "end": v(1499, 40) * mm});
            skLineSegment(sketch, "E37.4.0.2", {"start": v(1299, 1310) * mm, "end": v(1499, 1310) * mm});
            skLineSegment(sketch, "E37.4.0.3", {"start": v(1499, 1310) * mm, "end": v(1499, 40) * mm});
            skLineSegment(sketch, "E37.5.0.0", {"start": v(1557, 1310) * mm, "end": v(1557, 40) * mm});
            skLineSegment(sketch, "E37.5.0.1", {"start": v(1557, 40) * mm, "end": v(1757, 40) * mm});
            skLineSegment(sketch, "E37.5.0.2", {"start": v(1557, 1310) * mm, "end": v(1757, 1310) * mm});
            skLineSegment(sketch, "E37.5.0.3", {"start": v(1757, 1310) * mm, "end": v(1757, 40) * mm});
            skLineSegment(sketch, "E37.6.0.0", {"start": v(1815, 1310) * mm, "end": v(1815, 40) * mm});
            skLineSegment(sketch, "E37.6.0.1", {"start": v(1815, 40) * mm, "end": v(2015, 40) * mm});
            skLineSegment(sketch, "E37.6.0.2", {"start": v(1815, 1310) * mm, "end": v(2015, 1310) * mm});
            skLineSegment(sketch, "E37.6.0.3", {"start": v(2015, 1310) * mm, "end": v(2015, 40) * mm});
            skLineSegment(sketch, "E37.7.0.0", {"start": v(2073, 1310) * mm, "end": v(2073, 40) * mm});
            skLineSegment(sketch, "E37.7.0.1", {"start": v(2073, 40) * mm, "end": v(2273, 40) * mm});
            skLineSegment(sketch, "E37.7.0.2", {"start": v(2073, 1310) * mm, "end": v(2273, 1310) * mm});
            skLineSegment(sketch, "E37.7.0.3", {"start": v(2273, 1310) * mm, "end": v(2273, 40) * mm});
            skLineSegment(sketch, "E37.direction1", {"start": v(267, 40) * mm, "end": v(525, 40) * mm, "construction": true});
            skLineSegment(sketch, "E38.0.8.0", {"start": v(2331, 1310) * mm, "end": v(2331, 40) * mm});
            skLineSegment(sketch, "E38.3.8.0", {"start": v(2331, 40) * mm, "end": v(2531, 40) * mm});
            skLineSegment(sketch, "E38.6.8.0", {"start": v(2331, 1310) * mm, "end": v(2531, 1310) * mm});
            skLineSegment(sketch, "E38.9.8.0", {"start": v(2531, 1310) * mm, "end": v(2531, 40) * mm});
            skLineSegment(sketch, "E38.0.9.0", {"start": v(2589, 1310) * mm, "end": v(2589, 40) * mm});
            skLineSegment(sketch, "E38.3.9.0", {"start": v(2589, 40) * mm, "end": v(2789, 40) * mm});
            skLineSegment(sketch, "E38.6.9.0", {"start": v(2589, 1310) * mm, "end": v(2789, 1310) * mm});
            skLineSegment(sketch, "E38.9.9.0", {"start": v(2789, 1310) * mm, "end": v(2789, 40) * mm});
            skLineSegment(sketch, "E38.0.10.0", {"start": v(2847, 1310) * mm, "end": v(2847, 40) * mm});
            skLineSegment(sketch, "E38.3.10.0", {"start": v(2847, 40) * mm, "end": v(3047, 40) * mm});
            skLineSegment(sketch, "E38.6.10.0", {"start": v(2847, 1310) * mm, "end": v(3047, 1310) * mm});
            skLineSegment(sketch, "E38.9.10.0", {"start": v(3047, 1310) * mm, "end": v(3047, 40) * mm});
            skLineSegment(sketch, "E38.0.11.0", {"start": v(3105, 1310) * mm, "end": v(3105, 40) * mm});
            skLineSegment(sketch, "E38.3.11.0", {"start": v(3105, 40) * mm, "end": v(3305, 40) * mm});
            skLineSegment(sketch, "E38.6.11.0", {"start": v(3105, 1310) * mm, "end": v(3305, 1310) * mm});
            skLineSegment(sketch, "E38.9.11.0", {"start": v(3305, 1310) * mm, "end": v(3305, 40) * mm});
            skSolve(sketch);
        }
        {
            var Q0;
            Q0=makeQuery(id+"F8.imprint","IMPRINT",FACE,{"disambiguationData":[TD([[makeQuery(id+"F8.imprint","IMPRINT",EDGE,{"derivedFrom":sQuery(id+"F8.wireOp",EDGE,"E36.bottom")}),-1.0]])]});
            var Q1;
            Q1=makeQuery(id+"F8.imprint","IMPRINT",FACE,{"disambiguationData":[TD([[makeQuery(id+"F8.imprint","IMPRINT",EDGE,{"derivedFrom":sQuery(id+"F8.wireOp",EDGE,"E37.1.0.0")}),1.0]])]});
            var Q2;
            Q2=makeQuery(id+"F8.imprint","IMPRINT",FACE,{"disambiguationData":[TD([[makeQuery(id+"F8.imprint","IMPRINT",EDGE,{"derivedFrom":sQuery(id+"F8.wireOp",EDGE,"E37.2.0.0")}),1.0]])]});
            var Q3;
            Q3=makeQuery(id+"F8.imprint","IMPRINT",FACE,{"disambiguationData":[TD([[makeQuery(id+"F8.imprint","IMPRINT",EDGE,{"derivedFrom":sQuery(id+"F8.wireOp",EDGE,"E37.3.0.0")}),1.0]])]});
            var Q4;
            Q4=makeQuery(id+"F8.imprint","IMPRINT",FACE,{"disambiguationData":[TD([[makeQuery(id+"F8.imprint","IMPRINT",EDGE,{"derivedFrom":sQuery(id+"F8.wireOp",EDGE,"E37.4.0.0")}),1.0]])]});
            var Q5;
            Q5=makeQuery(id+"F8.imprint","IMPRINT",FACE,{"disambiguationData":[TD([[makeQuery(id+"F8.imprint","IMPRINT",EDGE,{"derivedFrom":sQuery(id+"F8.wireOp",EDGE,"E37.5.0.0")}),1.0]])]});
            var Q6;
            Q6=makeQuery(id+"F8.imprint","IMPRINT",FACE,{"disambiguationData":[TD([[makeQuery(id+"F8.imprint","IMPRINT",EDGE,{"derivedFrom":sQuery(id+"F8.wireOp",EDGE,"E37.6.0.0")}),1.0]])]});
            var Q7;
            Q7=makeQuery(id+"F8.imprint","IMPRINT",FACE,{"disambiguationData":[TD([[makeQuery(id+"F8.imprint","IMPRINT",EDGE,{"derivedFrom":sQuery(id+"F8.wireOp",EDGE,"E37.7.0.0")}),1.0]])]});
            var Q8;
            Q8=makeQuery(id+"F8.imprint","IMPRINT",FACE,{"disambiguationData":[TD([[makeQuery(id+"F8.imprint","IMPRINT",EDGE,{"derivedFrom":sQuery(id+"F8.wireOp",EDGE,"E38.0.8.0")}),1.0]])]});
            var Q9;
            Q9=makeQuery(id+"F8.imprint","IMPRINT",FACE,{"disambiguationData":[TD([[makeQuery(id+"F8.imprint","IMPRINT",EDGE,{"derivedFrom":sQuery(id+"F8.wireOp",EDGE,"E38.0.9.0")}),1.0]])]});
            var Q10;
            Q10=makeQuery(id+"F8.imprint","IMPRINT",FACE,{"disambiguationData":[TD([[makeQuery(id+"F8.imprint","IMPRINT",EDGE,{"derivedFrom":sQuery(id+"F8.wireOp",EDGE,"E38.0.10.0")}),1.0]])]});
            var Q11;
            Q11=makeQuery(id+"F8.imprint","IMPRINT",FACE,{"disambiguationData":[TD([[makeQuery(id+"F8.imprint","IMPRINT",EDGE,{"derivedFrom":sQuery(id+"F8.wireOp",EDGE,"E38.0.11.0")}),1.0]])]});
            extrude(context, id + "F9", {"entities" : qUnion([Q0, Q1, Q2, Q3, Q4, Q5, Q6, Q7, Q8, Q9, Q10, Q11]), "depth" : 10 * mm});
        }
    });
